# Revit family: Plumbing Fixture-Grease_Interseptor_Mifab_MI-G-L-SDH
name_source: partatom
category: Plumbing Fixtures
revit_build: Autodesk Revit Structure 2013 (Build: 20120221_2030(x64)
units: mm (PartAtom-declared; Revit-internal decimal feet)

## types (3) — shared parameters
Assembly Code = D2090300
C = 4 "
D = 7 "
Description = Semi-Automatic Grease Interceptors with Draw Off Hose
E = 11 "
F = 3 "
Floor Drain Material = Paint - Sherwin Williams Paint - #952C2A - Bellwood Red
Manufacturer = MIFAB
Standard Inlet And Outlet Radii = 1.5 "
zero-valued in all types: Default Elevation, WFU

## per-type parameters (varying)
| type | A | B | Flow Rate | Grease Capacity | Model | URL | Water Capacity |
| MI-G-L-SDH-20 | 36.5 " | 26.5 " | 20 GPM | 40 lbs | MI-G-L-SDH | www.mifab.com | 20.13 Gallons |
| MI-G-L-SDH-35 | 44.5 " | 30.5 " | 35 GPM | 70 lbs | MI-G-L-SDH-35 | WWW.MIFAB.COM | 28.84 Gallons |
| MI-G-L-SDH-50 | 48.5 " | 32.5 " | 50 GPM | 100 lbs | MI-G-L-SDH-50 | WWW.MIFAB.COM | 33.77 Gallons |

## geometry (parser evidence)
native form markers: Blend x3, Sweep x1
no freeform markers — native parametric forms only
